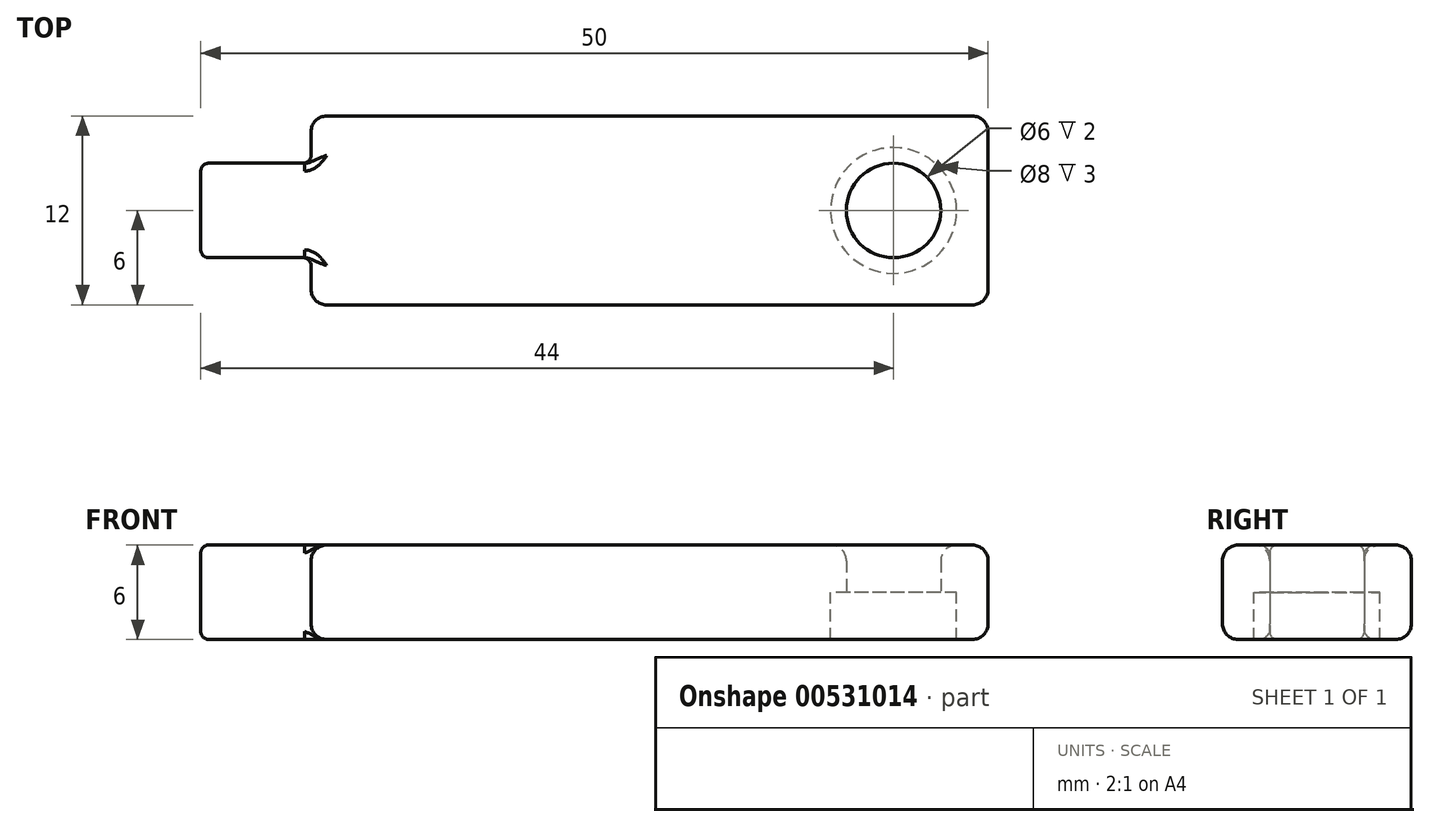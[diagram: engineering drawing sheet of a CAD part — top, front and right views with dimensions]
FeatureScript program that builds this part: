
annotation { "Feature Type Name" : "Feature", "Feature Type Description" : "" }
export const myFeature = defineFeature(function(context is Context, id is Id, definition is map)
    precondition{}
    {
        {
            var Q0;
            Q0=qCreatedBy(makeId("Top.planeOp"),FACE);
            var sketch = newSketch(context, id + "F0", { "sketchPlane" : qUnion([Q0])});
            skLineSegment(sketch, "E0", {"start": v(0, 3) * mm, "end": v(0, 0) * mm});
            skLineSegment(sketch, "E1", {"start": v(0, 0) * mm, "end": v(44, 0) * mm, "construction": true});
            skCircle(sketch, "E2", {"center": v(44, 0) * mm, "radius": 3 * mm});
            skCircle(sketch, "E3", {"center": v(44, 0) * mm, "radius": 4 * mm});
            skLineSegment(sketch, "E4", {"start": v(0, 3) * mm, "end": v(7, 3) * mm});
            skLineSegment(sketch, "E5", {"start": v(7, 3) * mm, "end": v(7, 6) * mm});
            skLineSegment(sketch, "E6", {"start": v(7, 6) * mm, "end": v(50, 6) * mm});
            skLineSegment(sketch, "E7", {"start": v(50, 6) * mm, "end": v(50, 0) * mm});
            skLineSegment(sketch, "E8.MirrorCS", {"start": v(0, -3) * mm, "end": v(0, 0) * mm});
            skLineSegment(sketch, "E9.MirrorCS", {"start": v(0, -3) * mm, "end": v(7, -3) * mm});
            skLineSegment(sketch, "E10.MirrorCS", {"start": v(7, -3) * mm, "end": v(7, -6) * mm});
            skLineSegment(sketch, "E11.MirrorCS", {"start": v(7, -6) * mm, "end": v(50, -6) * mm});
            skLineSegment(sketch, "E12.MirrorCS", {"start": v(50, -6) * mm, "end": v(50, 0) * mm});
            skSolve(sketch);
        }
        {
            var Q0;
            Q0 = qSketchRegion(id + "F0", true);
            var Q1;
            Q1=makeQuery(id+"F0.imprint","IMPRINT",FACE,{"disambiguationData":[TD([[makeQuery(id+"F0.imprint","IMPRINT",EDGE,{"derivedFrom":sQuery(id+"F0.wireOp",EDGE,"E2")}),-1.0]])]});
            extrude(context, id + "F1", {"entities" : qUnion([Q0, Q1]), "depth" : 3 * mm, "offsetDistance" : 25 * mm});
        }
        {
            var Q0;
            Q0 = qSketchRegion(id + "F0", true);
            extrude(context, id + "F2", {"entities" : qUnion([Q0]), "operationType" : NewBodyOperationType.ADD, "oppositeDirection" : true, "depth" : 3 * mm, "offsetDistance" : 25 * mm});
        }
        {
            var Q0;
            Q0=makeQuery(id+"F1.opExtrude","CAP_EDGE",EDGE,{"disambiguationData":[OSD([sQuery(id+"F0.wireOp",EDGE,"E2")])],"isStart":false});
            fillet(context, id + "F3", {"entities" : qUnion([Q0]), "radius" : 1 * mm, "tangentPropagation" : true, "allowEdgeOverflow" : false});
        }
        {
            var Q0;
            Q0=makeQuery(id+"F2.opExtrude","CAP_EDGE",EDGE,{"disambiguationData":[OSD([sQuery(id+"F0.wireOp",EDGE,"E11.MirrorCS")])],"isStart":false});
            var Q1;
            Q1=makeQuery(id+"F2.opExtrude","CAP_EDGE",EDGE,{"disambiguationData":[OSD([sQuery(id+"F0.wireOp",EDGE,"E7"),sQuery(id+"F0.wireOp",EDGE,"E12.MirrorCS")])],"isStart":false});
            var Q2;
            Q2=makeQuery(id+"F2.opExtrude","CAP_EDGE",EDGE,{"disambiguationData":[OSD([sQuery(id+"F0.wireOp",EDGE,"E6")])],"isStart":false});
            var Q3;
            Q3=makeQuery(id+"F2.opExtrude","CAP_EDGE",EDGE,{"disambiguationData":[OSD([sQuery(id+"F0.wireOp",EDGE,"E10.MirrorCS")])],"isStart":false});
            var Q4;
            Q4=makeQuery(id+"F2.opExtrude","CAP_EDGE",EDGE,{"disambiguationData":[OSD([sQuery(id+"F0.wireOp",EDGE,"E5")])],"isStart":false});
            var Q5;
            Q5=makeQuery(id+"F1.opExtrude","CAP_EDGE",EDGE,{"disambiguationData":[OSD([sQuery(id+"F0.wireOp",EDGE,"E6")])],"isStart":false});
            var Q6;
            Q6=makeQuery(id+"F1.opExtrude","CAP_EDGE",EDGE,{"disambiguationData":[OSD([sQuery(id+"F0.wireOp",EDGE,"E5")])],"isStart":false});
            var Q7;
            Q7=makeQuery(id+"F1.opExtrude","CAP_EDGE",EDGE,{"disambiguationData":[OSD([sQuery(id+"F0.wireOp",EDGE,"E7"),sQuery(id+"F0.wireOp",EDGE,"E12.MirrorCS")])],"isStart":false});
            var Q8;
            Q8=makeQuery(id+"F1.opExtrude","CAP_EDGE",EDGE,{"disambiguationData":[OSD([sQuery(id+"F0.wireOp",EDGE,"E11.MirrorCS")])],"isStart":false});
            var Q9;
            {var subQ0=sQuery(id+"F0.wireOp",EDGE,"E12.MirrorCS");var subQ1=sQuery(id+"F0.wireOp",EDGE,"E11.MirrorCS");Q9=makeQuery(id+"F2.boolean.opBoolean","MERGE",EDGE,{"derivedFrom":[makeQuery(id+"F1.opExtrude","SWEPT_EDGE",EDGE,{"disambiguationData":[OSD([subQ1,subQ0])]}),makeQuery(id+"F2.opExtrude","SWEPT_EDGE",EDGE,{"disambiguationData":[OSD([subQ1,subQ0])]})]});}
            var Q10;
            {var subQ0=sQuery(id+"F0.wireOp",EDGE,"E12.MirrorCS");var subQ1=sQuery(id+"F0.wireOp",EDGE,"E7");Q10=makeQuery(id+"F2.boolean.opBoolean","MERGE",FACE,{"derivedFrom":[makeQuery(id+"F1.opExtrude","SWEPT_FACE",FACE,{"disambiguationData":[OSD([subQ1,subQ0])]}),makeQuery(id+"F2.opExtrude","SWEPT_FACE",FACE,{"disambiguationData":[OSD([subQ1,subQ0])]})]});}
            var Q11;
            {var subQ0=sQuery(id+"F0.wireOp",EDGE,"E11.MirrorCS");var subQ1=sQuery(id+"F0.wireOp",EDGE,"E10.MirrorCS");Q11=makeQuery(id+"F2.boolean.opBoolean","MERGE",EDGE,{"derivedFrom":[makeQuery(id+"F1.opExtrude","SWEPT_EDGE",EDGE,{"disambiguationData":[OSD([subQ1,subQ0])]}),makeQuery(id+"F2.opExtrude","SWEPT_EDGE",EDGE,{"disambiguationData":[OSD([subQ1,subQ0])]})]});}
            var Q12;
            {var subQ0=sQuery(id+"F0.wireOp",EDGE,"E6");var subQ1=sQuery(id+"F0.wireOp",EDGE,"E5");Q12=makeQuery(id+"F2.boolean.opBoolean","MERGE",EDGE,{"derivedFrom":[makeQuery(id+"F1.opExtrude","SWEPT_EDGE",EDGE,{"disambiguationData":[OSD([subQ1,subQ0])]}),makeQuery(id+"F2.opExtrude","SWEPT_EDGE",EDGE,{"disambiguationData":[OSD([subQ1,subQ0])]})]});}
            var Q13;
            Q13=makeQuery(id+"F1.opExtrude","CAP_EDGE",EDGE,{"disambiguationData":[OSD([sQuery(id+"F0.wireOp",EDGE,"E10.MirrorCS")])],"isStart":false});
            fillet(context, id + "F4", {"entities" : qUnion([Q0, Q1, Q2, Q3, Q4, Q5, Q6, Q7, Q8, Q9, Q10, Q11, Q12, Q13]), "radius" : 1 * mm, "tangentPropagation" : true, "allowEdgeOverflow" : false});
        }
        {
            var Q0;
            Q0=makeQuery(id+"F1.opExtrude","CAP_EDGE",EDGE,{"disambiguationData":[OSD([sQuery(id+"F0.wireOp",EDGE,"E9.MirrorCS")])],"isStart":false});
            var Q1;
            Q1=makeQuery(id+"F1.opExtrude","CAP_EDGE",EDGE,{"disambiguationData":[OSD([sQuery(id+"F0.wireOp",EDGE,"E4")])],"isStart":false});
            var Q2;
            Q2=makeQuery(id+"F1.opExtrude","CAP_EDGE",EDGE,{"disambiguationData":[OSD([sQuery(id+"F0.wireOp",EDGE,"E0"),sQuery(id+"F0.wireOp",EDGE,"E8.MirrorCS")])],"isStart":false});
            var Q3;
            {var subQ0=sQuery(id+"F0.wireOp",EDGE,"E9.MirrorCS");var subQ1=sQuery(id+"F0.wireOp",EDGE,"E8.MirrorCS");Q3=makeQuery(id+"F2.boolean.opBoolean","MERGE",EDGE,{"derivedFrom":[makeQuery(id+"F1.opExtrude","SWEPT_EDGE",EDGE,{"disambiguationData":[OSD([subQ1,subQ0])]}),makeQuery(id+"F2.opExtrude","SWEPT_EDGE",EDGE,{"disambiguationData":[OSD([subQ1,subQ0])]})]});}
            var Q4;
            Q4=makeQuery(id+"F2.opExtrude","CAP_EDGE",EDGE,{"disambiguationData":[OSD([sQuery(id+"F0.wireOp",EDGE,"E9.MirrorCS")])],"isStart":false});
            var Q5;
            Q5=makeQuery(id+"F2.opExtrude","CAP_EDGE",EDGE,{"disambiguationData":[OSD([sQuery(id+"F0.wireOp",EDGE,"E0"),sQuery(id+"F0.wireOp",EDGE,"E8.MirrorCS")])],"isStart":false});
            var Q6;
            {var subQ0=sQuery(id+"F0.wireOp",EDGE,"E4");var subQ1=sQuery(id+"F0.wireOp",EDGE,"E0");Q6=makeQuery(id+"F2.boolean.opBoolean","MERGE",EDGE,{"derivedFrom":[makeQuery(id+"F1.opExtrude","SWEPT_EDGE",EDGE,{"disambiguationData":[OSD([subQ1,subQ0])]}),makeQuery(id+"F2.opExtrude","SWEPT_EDGE",EDGE,{"disambiguationData":[OSD([subQ1,subQ0])]})]});}
            var Q7;
            Q7=makeQuery(id+"F2.opExtrude","CAP_EDGE",EDGE,{"disambiguationData":[OSD([sQuery(id+"F0.wireOp",EDGE,"E4")])],"isStart":false});
            var Q8;
            {var subQ0=sQuery(id+"F0.wireOp",EDGE,"E4");Q8=makeQuery(id+"F2.boolean.opBoolean","MERGE",FACE,{"derivedFrom":[makeQuery(id+"F1.opExtrude","SWEPT_FACE",FACE,{"disambiguationData":[OSD([subQ0])]}),makeQuery(id+"F2.opExtrude","SWEPT_FACE",FACE,{"disambiguationData":[OSD([subQ0])]})]});}
            var Q9;
            {var subQ0=sQuery(id+"F0.wireOp",EDGE,"E9.MirrorCS");Q9=makeQuery(id+"F2.boolean.opBoolean","MERGE",FACE,{"derivedFrom":[makeQuery(id+"F1.opExtrude","SWEPT_FACE",FACE,{"disambiguationData":[OSD([subQ0])]}),makeQuery(id+"F2.opExtrude","SWEPT_FACE",FACE,{"disambiguationData":[OSD([subQ0])]})]});}
            fillet(context, id + "F5", {"entities" : qUnion([Q0, Q1, Q2, Q3, Q4, Q5, Q6, Q7, Q8, Q9]), "radius" : 0.5 * mm, "tangentPropagation" : true, "allowEdgeOverflow" : false});
        }
    });
